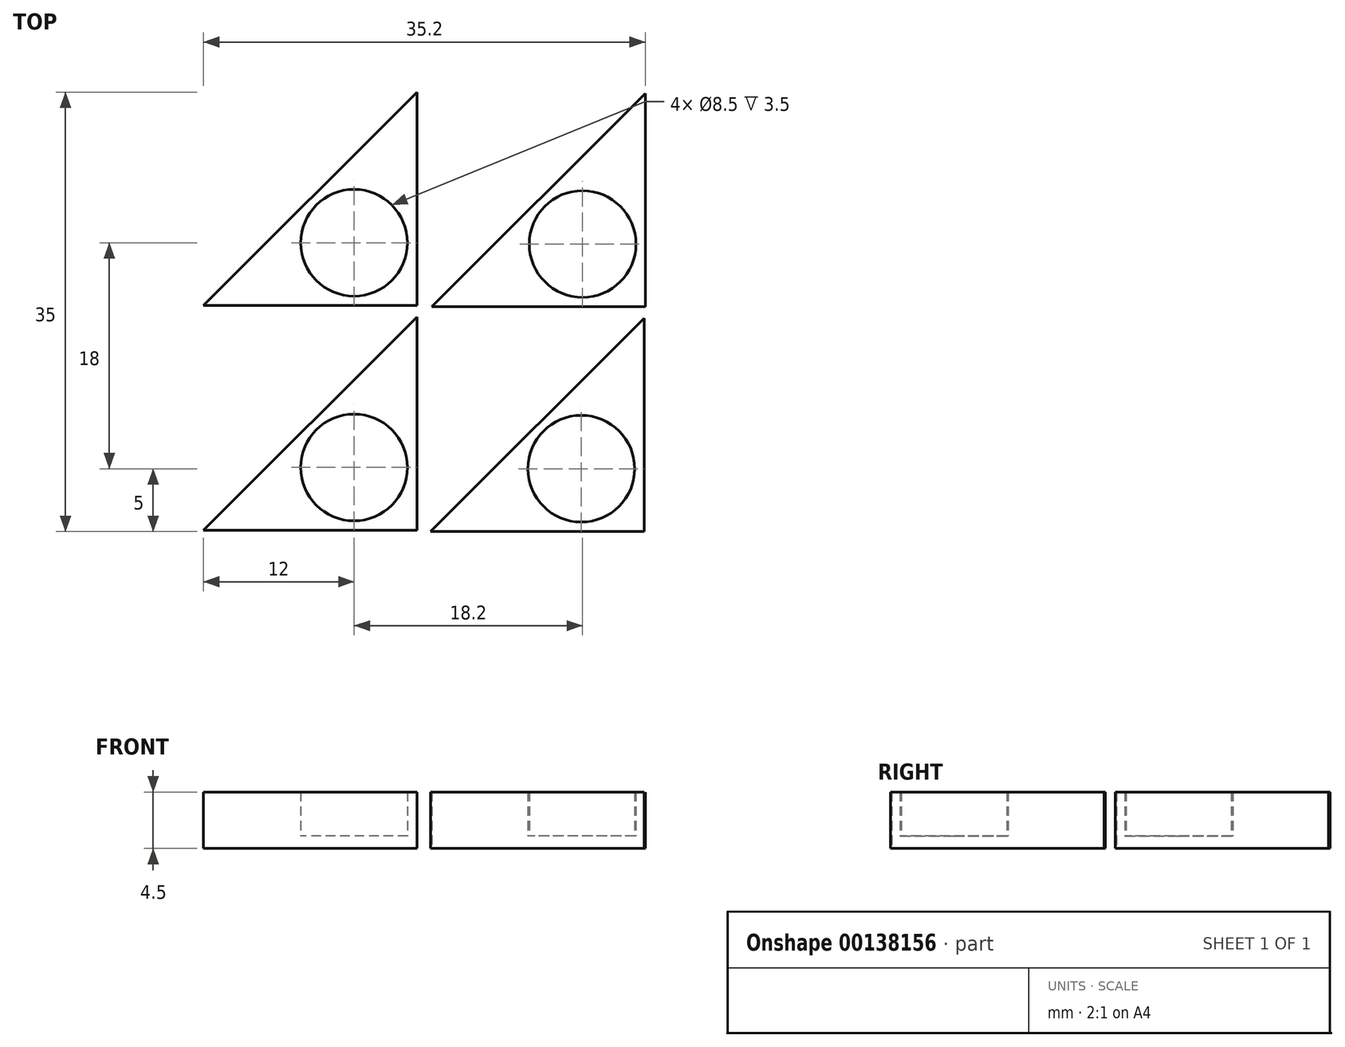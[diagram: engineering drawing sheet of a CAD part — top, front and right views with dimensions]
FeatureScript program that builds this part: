
annotation { "Feature Type Name" : "Feature", "Feature Type Description" : "" }
export const myFeature = defineFeature(function(context is Context, id is Id, definition is map)
    precondition{}
    {
        {
            var Q0;
            Q0=qCreatedBy(makeId("Top.planeOp"),FACE);
            var sketch = newSketch(context, id + "F0", { "sketchPlane" : qUnion([Q0])});
            skLineSegment(sketch, "E0", {"start": v(0, 0) * mm, "end": v(0, 17) * mm});
            skLineSegment(sketch, "E1", {"start": v(0, 0) * mm, "end": v(-17, 0) * mm});
            skCircle(sketch, "E2", {"center": v(-5, 5) * mm, "radius": 4.25 * mm});
            skLineSegment(sketch, "E3", {"start": v(0, 17) * mm, "end": v(-17, 0) * mm});
            skSolve(sketch);
        }
        {
            var Q0;
            Q0=makeQuery(id+"F0.imprint","IMPRINT",FACE,{"disambiguationData":[TD([[makeQuery(id+"F0.imprint","IMPRINT",EDGE,{"derivedFrom":sQuery(id+"F0.wireOp",EDGE,"E0")}),1.0]])]});
            extrude(context, id + "F1", {"entities" : qUnion([Q0]), "depth" : 4.5 * mm});
        }
        {
            var Q0;
            Q0=makeQuery(id+"F0.imprint","IMPRINT",FACE,{"disambiguationData":[TD([[makeQuery(id+"F0.imprint","IMPRINT",EDGE,{"derivedFrom":sQuery(id+"F0.wireOp",EDGE,"E2")}),1.0]])]});
            extrude(context, id + "F2", {"entities" : qUnion([Q0]), "operationType" : NewBodyOperationType.ADD, "depth" : 1 * mm});
        }
        {
            var Q0;
            Q0=makeQuery(id+"F1.opExtrude","SWEPT_BODY",BODY,{"disambiguationData":[OSD([sQuery(id+"F0.wireOp",EDGE,"E0"),sQuery(id+"F0.wireOp",EDGE,"E1"),sQuery(id+"F0.wireOp",EDGE,"E2"),sQuery(id+"F0.wireOp",EDGE,"E3")])]});
            transform(context, id + "F3", {"entities" : qUnion([Q0]), "transformType" : TransformType.TRANSLATION_3D, "dx" : 18.2 * mm, "dy" : -0.1 * mm, "dz" : 0 * mm, "makeCopy" : true});
        }
        {
            var Q0;
            Q0=makeQuery(id+"F1.opExtrude","SWEPT_BODY",BODY,{"disambiguationData":[OSD([sQuery(id+"F0.wireOp",EDGE,"E0"),sQuery(id+"F0.wireOp",EDGE,"E1"),sQuery(id+"F0.wireOp",EDGE,"E2"),sQuery(id+"F0.wireOp",EDGE,"E3")])]});
            transform(context, id + "F4", {"entities" : qUnion([Q0]), "transformType" : TransformType.TRANSLATION_3D, "dx" : 0 * mm, "dy" : -17.9 * mm, "dz" : 0 * mm, "makeCopy" : true});
        }
        {
            var Q0;
            Q0=makeQuery(id+"F1.opExtrude","SWEPT_BODY",BODY,{"disambiguationData":[OSD([sQuery(id+"F0.wireOp",EDGE,"E0"),sQuery(id+"F0.wireOp",EDGE,"E1"),sQuery(id+"F0.wireOp",EDGE,"E2"),sQuery(id+"F0.wireOp",EDGE,"E3")])]});
            transform(context, id + "F5", {"entities" : qUnion([Q0]), "transformType" : TransformType.TRANSLATION_3D, "dx" : 18.1 * mm, "dy" : -18 * mm, "dz" : 0 * mm, "makeCopy" : true});
        }
    });
